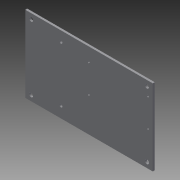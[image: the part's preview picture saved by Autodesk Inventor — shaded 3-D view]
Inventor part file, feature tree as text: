
AUTODESK INVENTOR PART (.ipt)
format: ipt  version: 2014 (Build 180170000, 170)  size: 119,296 bytes
history: native  units: mm
features: extrude x3, sketch x3
ambient origin geometry x8: Origin, YZ Plane, XZ Plane, XY Plane, X Axis, Y Axis, Z Axis, Center Point
bodies: Solid1 (feature_tree)
feature tree (6):
  extrude  "Extrusion1"  Depth=127.0mm
  extrude  "Extrusion2"  Depth=2.0mm
  extrude  "Extrusion3"  Depth=10.0mm
  sketch  "Sketch1"  dims[d0=76.0mm d1=127.0mm]
  sketch  "Sketch2"  dims[d2=2.0mm d3=0.0mm d5=32.6mm]
  sketch  "Sketch3"  dims[d6=57.7mm d7=4.0mm d8=10.0mm d9=0.0mm d10=93.0mm d12=51.0mm d13=10.0mm d14=63.0mm d15=35.0mm d16=11.0mm d17=3.0mm d18=20.0mm d20=55.0mm d21=10.0mm d23=10.0mm d25=32.0mm d26=29.5mm d27=2.0mm d28=15.0mm d29=20.0mm d31=28.0mm d32=20.0mm d34=58.9mm d37=10.0mm d38=0.0mm]
